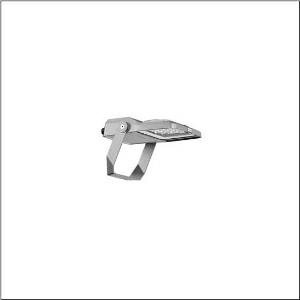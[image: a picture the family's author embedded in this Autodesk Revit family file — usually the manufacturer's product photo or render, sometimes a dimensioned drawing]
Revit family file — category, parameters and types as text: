
# Revit family: floodlight_fl_21_iq_micro___rsd12_5xa7762a4b1a_7d54
name_source: partatom
category: Lighting Fixtures
units: mm (PartAtom-declared; Revit-internal decimal feet)

## family parameters
Cut with Voids When Loaded = No
Host = Face
Light Source = No
Part Type = Normal
Room Calculation Point = No
Round Connector Dimension = Use Diameter
Shared = No

## types (1)
- --- (1 x LED, 3220 lm, 23.1 W, 4000K)
    Apparent Load = 23 VA
    CIE Flux Codes = 79 92 99 100 100
    Color Rendering = 70
    Color Temperature = 4000K
    Default Elevation = 1800 mm
    Description = Floodlight FL 21 iQ micro, floodlight, primary light control with lens, of PMMA, primary optical cover: protective disc, of toughened safety glass, transparent, light distribution: RSD12, light emission: direct distribution, installation type: surface-mounted, LED, High Power LED, rated luminous flux: 3.220lm, luminous efficacy: 139lm/W, light colour: 740, colour temperature: 4000K, control gear: iQ Street-Remote/DALI, control: Auto-Match, Temp-Guard, Night-Set, Smart-Wire, Desk-Remote (wireless, voltage-free reading and setting of iQ features in the workshop via application-optimized NFC function/RFID function), optimised constant luminous flux control (CLO 2.0), Street-Remote, with terminal, 6-pole, mains connection: 220..240V, AC, 50/60Hz, start of lifetime: 23W, end of service life: 24W, reduction: 11W, luminaire housing, of diecast aluminium, powder-coated, Siteco® metallic grey (DB 702S), corrosivity category C5 mid according to DIN EN ISO 12944, suitable for swimming pools, chlorine-resistant, sealing non-destructively replaceable, mounting bracket, of steel, galvanised, powder-coated, Siteco® metallic grey (DB 702S), protection rating (complete): IP66, insulation class (complete): insulation class II (safety insulation), certification: CE, ENEC, VDE, protection symbol: D, impact resistance: IK07, permissible operating ambient temperature: -40..+40°C, permissible operating ambient temperature for outdoor applications: -40..+50°C, standard: DIN EN 12944, LABS conformity tested according to VDMA 24364:2018-05, packaging unit: 1 piece

Light Distribution: RSD12
    Height = 65 mm
    Lamp = 1 x LED
    Lamp Light Flux = 3220 lm
    Lamp Power = 23.1 W
    Lamp count = 1
    Length = 312 mm
    Luminous efficacy = 139 lm/W
    Manufacturer = Siteco
    ModVariant = No
    Model = 5XA7762A4B1A
    Mounting Place = Wall
    Mounting Type = Surface mounted
    Number of Poles = 1
    OnlyDefault = Yes
    Power Factor = 1
    Product Name = Floodlight FL 21 iQ micro | RSD12
    Product group = floodlight | wall mounted
    ProductGroupID = 2001
    Protection Class = Protection class II
    Protection Degree = IP 66
    RLX_Detail_Level = 1
    RLX_Emergency_Light_Flux = 0 lm
    RLX_Emergency_Type = 0
    RLX_Emergency_Type_DB = No
    RlxData = <blob elided: 75401 chars, md5=71fcbb27>
    Socket = socket
    Standby Power = 0 W
    System Light Flux = 3220 lm
    System Power = 23 W
    Type Comments = factory setting: luminous flux: 100 % | dim-lin: 254 | 455 mA
    Type Image = l_1006880.jpg
    URL = http://relux.com
    VarID = @adj_181786
    Voltage = 0 V
    Weight = 0.00 kg
    Width = 230 mm

## geometry (parser evidence)
native form markers: Blend x4, Sweep x12
no freeform markers — native parametric forms only
